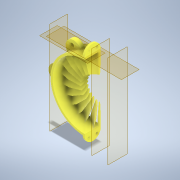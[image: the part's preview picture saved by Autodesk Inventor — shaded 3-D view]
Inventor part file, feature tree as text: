
AUTODESK INVENTOR PART (.ipt)
format: ipt  version: 2021.2 (Build 252289000, 289)  size: 1,438,720 bytes
history: native  units: in
note: dims shown in document units (in); Inventor stores cm internally (conversion verified against a paired STEP export)
features: sketch x11, extrude x10, plane x5, pattern_circular x3, fillet x2, loft x1, other x1
ambient origin geometry x8: Origin, YZ Plane, XZ Plane, XY Plane, X Axis, Y Axis, Z Axis, Center Point
bodies: Solid1 (feature_tree)
feature tree (33):
  extrude  "Extrusion1"  Depth=4.25in
  plane  "Work Plane2"
  extrude  "Extrusion3"  Depth=2.125in
  fillet  "Fillet1"  Radius=0.25in
  extrude  "Extrusion4"  Depth=0.5in TaperAngle=0.0deg
  pattern_circular  "Circular Pattern2"  Count=2 Angle=360.0deg
  plane  "Work Plane3"
  extrude  "Extrusion5"  Depth=1.0in
  extrude  "Extrusion6"  Depth=0.5in
  fillet  "Fillet2"  [1 undecoded]
  extrude  "Extrusion7"  Depth=0.5in TaperAngle=0.0deg
  pattern_circular  "Circular Pattern3"  [2 undecoded]
  plane  "Work Plane4"
  plane  "Work Plane6"
  sketch  "Sketch13"  dims[d18=0.5in d19=0.0in d20=0.7874in d21=360.0deg]
  extrude  "Extrusion15"  Depth=2.0in
  loft  "Loft5"
  pattern_circular  "Circular Pattern9"  Count=6 Angle=360.0deg
  extrude  "Extrusion16"  Depth=2.0in
  extrude  "Extrusion17"  Depth=0.125in
  plane  "Work Plane7"
  extrude  "Extrusion18"  Depth=2.0in
  sketch  "Sketch1"  dims[d0=4.0in d1=4.25in]
  sketch  "Sketch3"  dims[d2=1.0in d3=0.0in d10=2.125in d11=0.25in]
  sketch  "Sketch4"  dims[d12=0.0in d13=0.5in d14=0.0in]
  sketch  "Sketch5"  dims[d15=0.5in]
  sketch  "Sketch6"  dims[d16=0.125in]
  sketch  "Sketch7"  dims[d17=0.2in]
  sketch  "Sketch16"  dims[d23=-2.125in d24=1.0in]
  other  "Edges5"
  sketch  "Sketch18"  dims[d25=0.25in d26=0.5in d27=0.0in]
  sketch  "Sketch19"  dims[d28=0.1in d29=0.0in d30=0.5in d31=0.0in]
  sketch  "Sketch20"  dims[d32=0.5in d33=0.25in d34=0.2in d35=0.5in d36=0.0in d37=2.3622in d38=360.0deg d40=0.25in d41=0.125in d42=0.25in d43=0.2in d49=0.5in d75=1.5in d111=0.5in d112=0.0312in d113=0.5in d114=0.0in d115=0.0in d116=90.0deg d117=0.0in d118=90.0deg d119=9.4488in d120=360.0deg d122=1.4625in d123=0.0in d124=0.0777in d125=0.0in d126=0.0in d127=1.95in d128=2.0in d129=0.0in d79=0.5in d80=0.0344in d81=0.5in d82=0.0344in]
note: 3 required parameter values undecoded (feature->parameter linkage not recoverable at this tier; creation-order binding heuristic only, values carry confidence <= 0.55)
